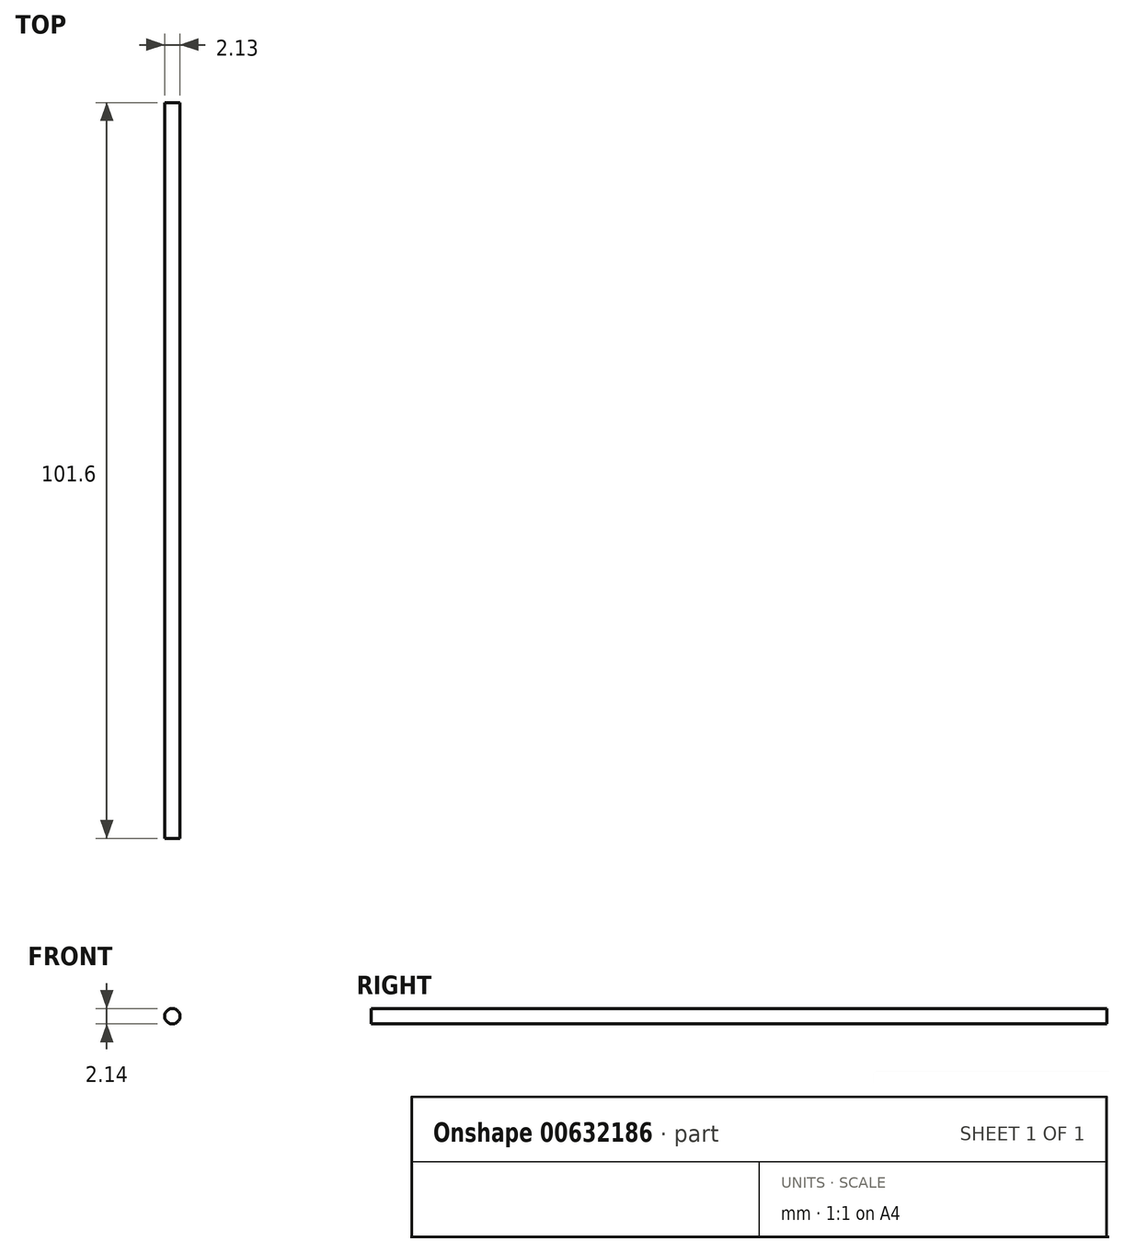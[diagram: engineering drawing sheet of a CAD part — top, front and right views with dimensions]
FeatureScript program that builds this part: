
annotation { "Feature Type Name" : "Feature", "Feature Type Description" : "" }
export const myFeature = defineFeature(function(context is Context, id is Id, definition is map)
    precondition{}
    {
        {
            var Q0;
            Q0=qCreatedBy(makeId("Front.planeOp"),FACE);
            var sketch = newSketch(context, id + "F0", { "sketchPlane" : qUnion([Q0])});
            skCircle(sketch, "E0", {"center": v(-29.63, 23.82) * mm, "radius": 1.07 * mm});
            skSolve(sketch);
        }
        {
            var Q0;
            Q0=makeQuery(id+"F0.imprint","IMPRINT",FACE,{"disambiguationData":[TD([[makeQuery(id+"F0.imprint","IMPRINT",EDGE,{"derivedFrom":sQuery(id+"F0.wireOp",EDGE,"E0")}),1.0]])]});
            extrude(context, id + "F1", {"entities" : qUnion([Q0]), "depth" : 101.6 * mm, "offsetDistance" : 25.4 * mm});
        }
    });
